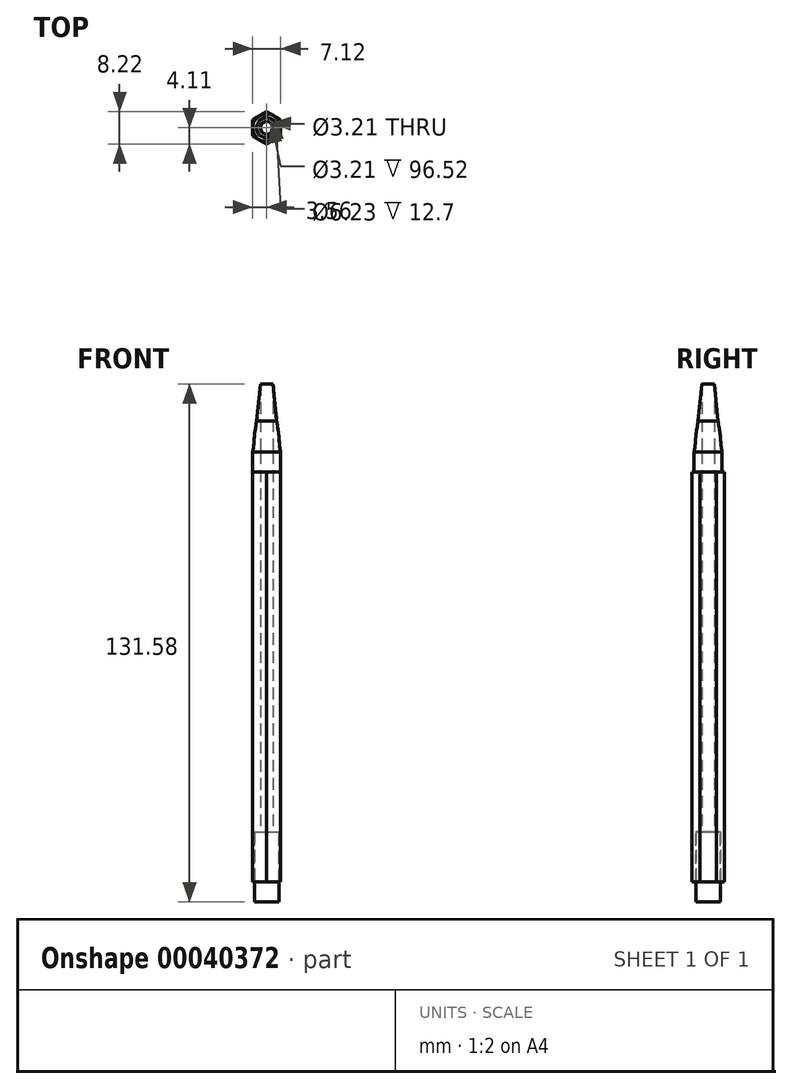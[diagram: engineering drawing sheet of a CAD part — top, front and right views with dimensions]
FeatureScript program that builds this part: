
annotation { "Feature Type Name" : "Feature", "Feature Type Description" : "" }
export const myFeature = defineFeature(function(context is Context, id is Id, definition is map)
    precondition{}
    {
        {
            var Q0;
            Q0=qCreatedBy(makeId("Top.planeOp"),FACE);
            var sketch = newSketch(context, id + "F0", { "sketchPlane" : qUnion([Q0])});
            skCircle(sketch, "E0.cCircle", {"center": v(0, 0) * mm, "radius": 3.56 * mm, "construction": true});
            skLineSegment(sketch, "E0.0", {"start": v(-3.56, 2.05) * mm, "end": v(0, 4.1) * mm});
            skLineSegment(sketch, "E0.1", {"start": v(0, 4.1) * mm, "end": v(3.55, 2.06) * mm});
            skLineSegment(sketch, "E0.2", {"start": v(3.55, 2.06) * mm, "end": v(3.56, -2.05) * mm});
            skLineSegment(sketch, "E0.3", {"start": v(3.56, -2.05) * mm, "end": v(0, -4.1) * mm});
            skLineSegment(sketch, "E0.4", {"start": v(0, -4.1) * mm, "end": v(-3.55, -2.06) * mm});
            skLineSegment(sketch, "E0.5", {"start": v(-3.55, -2.06) * mm, "end": v(-3.56, 2.05) * mm});
            skPoint(sketch, "E0.0.midPoint", {"position": v(-1.78, 3.08) * mm});
            skSolve(sketch);
        }
        {
            var Q0;
            Q0 = qSketchRegion(id + "F0", true);
            extrude(context, id + "F1", {"entities" : qUnion([Q0]), "depth" : 104.14 * mm});
        }
        {
            var Q0;
            Q0=makeQuery(id+"F1.opExtrude","CAP_FACE",FACE,{"disambiguationData":[OSD([sQuery(id+"F0.wireOp",EDGE,"E0.0"),sQuery(id+"F0.wireOp",EDGE,"E0.1"),sQuery(id+"F0.wireOp",EDGE,"E0.2"),sQuery(id+"F0.wireOp",EDGE,"E0.3"),sQuery(id+"F0.wireOp",EDGE,"E0.4"),sQuery(id+"F0.wireOp",EDGE,"E0.5")])],"isStart":false});
            var sketch = newSketch(context, id + "F2", { "sketchPlane" : qUnion([Q0])});
            skCircle(sketch, "E1", {"center": v(0, 0) * mm, "radius": 3.56 * mm});
            skSolve(sketch);
        }
        {
            var Q0;
            Q0 = qSketchRegion(id + "F2", true);
            extrude(context, id + "F3", {"entities" : qUnion([Q0]), "operationType" : NewBodyOperationType.ADD, "depth" : 5.08 * mm});
        }
        {
            var Q0;
            Q0=makeQuery(id+"F3.opExtrude","CAP_FACE",FACE,{"disambiguationData":[OSD([sQuery(id+"F2.wireOp",EDGE,"E1")])],"isStart":false});
            cPlane(context, id + "F4", {"entities" : qUnion([Q0]), "cplaneType" : CPlaneType.OFFSET, "offset" : 1.59 * mm, "width" : 152.4 * mm, "height" : 152.4 * mm});
        }
        {
            var Q0;
            Q0=qCreatedBy(id+"F4.planeOp",FACE);
            cPlane(context, id + "F5", {"entities" : qUnion([Q0]), "cplaneType" : CPlaneType.OFFSET, "offset" : 1.59 * mm, "width" : 152.4 * mm, "height" : 152.4 * mm});
        }
        {
            var Q0;
            Q0=qCreatedBy(id+"F5.planeOp",FACE);
            cPlane(context, id + "F6", {"entities" : qUnion([Q0]), "cplaneType" : CPlaneType.OFFSET, "offset" : 1.59 * mm, "width" : 152.4 * mm, "height" : 152.4 * mm});
        }
        {
            var Q0;
            Q0=qCreatedBy(id+"F6.planeOp",FACE);
            cPlane(context, id + "F7", {"entities" : qUnion([Q0]), "cplaneType" : CPlaneType.OFFSET, "offset" : 1.59 * mm, "width" : 152.4 * mm, "height" : 152.4 * mm});
        }
        {
            var Q0;
            Q0=qCreatedBy(id+"F7.planeOp",FACE);
            cPlane(context, id + "F8", {"entities" : qUnion([Q0]), "cplaneType" : CPlaneType.OFFSET, "offset" : 1.59 * mm, "width" : 152.4 * mm, "height" : 152.4 * mm});
        }
        {
            var Q0;
            Q0=qCreatedBy(id+"F8.planeOp",FACE);
            cPlane(context, id + "F9", {"entities" : qUnion([Q0]), "cplaneType" : CPlaneType.OFFSET, "offset" : 1.59 * mm, "width" : 152.4 * mm, "height" : 152.4 * mm});
        }
        {
            var Q0;
            Q0=qCreatedBy(id+"F9.planeOp",FACE);
            cPlane(context, id + "F10", {"entities" : qUnion([Q0]), "cplaneType" : CPlaneType.OFFSET, "offset" : 1.59 * mm, "width" : 152.4 * mm, "height" : 152.4 * mm});
        }
        {
            var Q0;
            Q0=qCreatedBy(id+"F10.planeOp",FACE);
            cPlane(context, id + "F11", {"entities" : qUnion([Q0]), "cplaneType" : CPlaneType.OFFSET, "offset" : 1.59 * mm, "width" : 152.4 * mm, "height" : 152.4 * mm});
        }
        {
            var Q0;
            Q0=qCreatedBy(id+"F11.planeOp",FACE);
            cPlane(context, id + "F12", {"entities" : qUnion([Q0]), "cplaneType" : CPlaneType.OFFSET, "offset" : 1.59 * mm, "width" : 152.4 * mm, "height" : 152.4 * mm});
        }
        {
            var Q0;
            Q0=qCreatedBy(id+"F12.planeOp",FACE);
            cPlane(context, id + "F13", {"entities" : qUnion([Q0]), "cplaneType" : CPlaneType.OFFSET, "offset" : 1.59 * mm, "width" : 152.4 * mm, "height" : 152.4 * mm});
        }
        {
            var Q0;
            Q0=qCreatedBy(id+"F13.planeOp",FACE);
            cPlane(context, id + "F14", {"entities" : qUnion([Q0]), "cplaneType" : CPlaneType.OFFSET, "offset" : 1.59 * mm, "width" : 152.4 * mm, "height" : 152.4 * mm});
        }
        {
            var Q0;
            Q0=qCreatedBy(id+"F14.planeOp",FACE);
            cPlane(context, id + "F15", {"entities" : qUnion([Q0]), "cplaneType" : CPlaneType.OFFSET, "offset" : 1.59 * mm, "width" : 152.4 * mm, "height" : 152.4 * mm});
        }
        {
            var Q0;
            Q0=qCreatedBy(id+"F15.planeOp",FACE);
            cPlane(context, id + "F16", {"entities" : qUnion([Q0]), "cplaneType" : CPlaneType.OFFSET, "offset" : 1.59 * mm, "width" : 152.4 * mm, "height" : 152.4 * mm});
        }
        {
            var Q0;
            Q0=qCreatedBy(id+"F16.planeOp",FACE);
            cPlane(context, id + "F17", {"entities" : qUnion([Q0]), "cplaneType" : CPlaneType.OFFSET, "offset" : 1.59 * mm, "width" : 152.4 * mm, "height" : 152.4 * mm});
        }
        {
            var Q0;
            Q0=qCreatedBy(id+"F17.planeOp",FACE);
            cPlane(context, id + "F18", {"entities" : qUnion([Q0]), "cplaneType" : CPlaneType.OFFSET, "offset" : 1.59 * mm, "width" : 152.4 * mm, "height" : 152.4 * mm});
        }
        {
            var Q0;
            Q0=qCreatedBy(id+"F18.planeOp",FACE);
            cPlane(context, id + "F19", {"entities" : qUnion([Q0]), "cplaneType" : CPlaneType.OFFSET, "offset" : 1.59 * mm, "width" : 152.4 * mm, "height" : 152.4 * mm});
        }
        {
            var Q0;
            Q0=qCreatedBy(id+"F4.planeOp",FACE);
            var sketch = newSketch(context, id + "F20", { "sketchPlane" : qUnion([Q0])});
            skCircle(sketch, "E2", {"center": v(0, 0) * mm, "radius": 3.3 * mm});
            skSolve(sketch);
        }
        {
            var Q0;
            Q0=qCreatedBy(id+"F5.planeOp",FACE);
            var sketch = newSketch(context, id + "F21", { "sketchPlane" : qUnion([Q0])});
            skCircle(sketch, "E3", {"center": v(0, 0) * mm, "radius": 3.18 * mm});
            skSolve(sketch);
        }
        {
            var Q0;
            Q0=qCreatedBy(id+"F6.planeOp",FACE);
            var sketch = newSketch(context, id + "F22", { "sketchPlane" : qUnion([Q0])});
            skCircle(sketch, "E4", {"center": v(0, 0) * mm, "radius": 3.05 * mm});
            skSolve(sketch);
        }
        {
            var Q0;
            Q0=qCreatedBy(id+"F6.planeOp",FACE);
            var sketch = newSketch(context, id + "F23", { "sketchPlane" : qUnion([Q0])});
            skCircle(sketch, "E5", {"center": v(0, 0) * mm, "radius": 2.92 * mm});
            skSolve(sketch);
        }
        {
            var Q0;
            Q0=qCreatedBy(id+"F7.planeOp",FACE);
            var sketch = newSketch(context, id + "F24", { "sketchPlane" : qUnion([Q0])});
            skCircle(sketch, "E6", {"center": v(0, 0) * mm, "radius": 2.8 * mm});
            skSolve(sketch);
        }
        {
            var Q0;
            Q0=qCreatedBy(id+"F8.planeOp",FACE);
            var sketch = newSketch(context, id + "F25", { "sketchPlane" : qUnion([Q0])});
            skCircle(sketch, "E7", {"center": v(0, 0) * mm, "radius": 2.54 * mm});
            skSolve(sketch);
        }
        {
            var Q0;
            Q0=makeQuery(id+"F3.opExtrude","CAP_FACE",FACE,{"disambiguationData":[OSD([sQuery(id+"F2.wireOp",EDGE,"E1")])],"isStart":false});
            var Q1;
            Q1=makeQuery(id+"F20.imprint","IMPRINT",FACE,{"disambiguationData":[TD([[makeQuery(id+"F20.imprint","IMPRINT",EDGE,{"derivedFrom":sQuery(id+"F20.wireOp",EDGE,"E2")}),1.0]])]});
            var Q2;
            Q2=makeQuery(id+"F21.imprint","IMPRINT",FACE,{"disambiguationData":[TD([[makeQuery(id+"F21.imprint","IMPRINT",EDGE,{"derivedFrom":sQuery(id+"F21.wireOp",EDGE,"E3")}),1.0]])]});
            var Q3;
            Q3=makeQuery(id+"F22.imprint","IMPRINT",FACE,{"disambiguationData":[TD([[makeQuery(id+"F22.imprint","IMPRINT",EDGE,{"derivedFrom":sQuery(id+"F22.wireOp",EDGE,"E4")}),1.0]])]});
            var Q4;
            Q4=makeQuery(id+"F24.imprint","IMPRINT",FACE,{"disambiguationData":[TD([[makeQuery(id+"F24.imprint","IMPRINT",EDGE,{"derivedFrom":sQuery(id+"F24.wireOp",EDGE,"E6")}),1.0]])]});
            var Q5;
            Q5=makeQuery(id+"F25.imprint","IMPRINT",FACE,{"disambiguationData":[TD([[makeQuery(id+"F25.imprint","IMPRINT",EDGE,{"derivedFrom":sQuery(id+"F25.wireOp",EDGE,"E7")}),1.0]])]});
            loft(context, id + "F26", {"sheetProfilesArray" : [{ "sheetProfileEntities" : qUnion([Q0]) }, { "sheetProfileEntities" : qUnion([Q1]) }, { "sheetProfileEntities" : qUnion([Q2]) }, { "sheetProfileEntities" : qUnion([Q3]) }, { "sheetProfileEntities" : qUnion([Q4]) }, { "sheetProfileEntities" : qUnion([Q5]) }]});
        }
        {
            var Q0;
            Q0=qCreatedBy(id+"F19.planeOp",FACE);
            var sketch = newSketch(context, id + "F27", { "sketchPlane" : qUnion([Q0])});
            skCircle(sketch, "E8", {"center": v(0, 0) * mm, "radius": 0.8 * mm});
            skSolve(sketch);
        }
        {
            var Q1;
            Q1=makeQuery(id+"F26.opLoft","CAP_FACE",FACE,{"disambiguationData":[OSD([makeQuery(id+"F25.imprint","IMPRINT",FACE,{"disambiguationData":[TD([[makeQuery(id+"F25.imprint","IMPRINT",EDGE,{"derivedFrom":sQuery(id+"F25.wireOp",EDGE,"E7")}),1.0]])]})])],"isStart":true});
            var Q2;
            Q2=makeQuery(id+"F27.imprint","IMPRINT",FACE,{"disambiguationData":[TD([[makeQuery(id+"F27.imprint","IMPRINT",EDGE,{"derivedFrom":sQuery(id+"F27.wireOp",EDGE,"E8")}),1.0]])]});
            loft(context, id + "F28", {"operationType" : NewBodyOperationType.ADD, "sheetProfilesArray" : [{ "sheetProfileEntities" : qUnion([Q1]) }, { "sheetProfileEntities" : qUnion([Q2]) }]});
        }
        {
            var Q0;
            Q0=makeQuery(id+"F28.opLoft","CAP_FACE",FACE,{"disambiguationData":[OSD([makeQuery(id+"F27.imprint","IMPRINT",FACE,{"disambiguationData":[TD([[makeQuery(id+"F27.imprint","IMPRINT",EDGE,{"derivedFrom":sQuery(id+"F27.wireOp",EDGE,"E8")}),1.0]])]})])],"isStart":true});
            var sketch = newSketch(context, id + "F29", { "sketchPlane" : qUnion([Q0])});
            skCircle(sketch, "E9", {"center": v(0, 0) * mm, "radius": 0.47 * mm});
            skSolve(sketch);
        }
        {
            var Q0;
            Q0 = qSketchRegion(id + "F29", true);
            extrude(context, id + "F30", {"entities" : qUnion([Q0]), "operationType" : NewBodyOperationType.REMOVE, "endBound" : BoundingType.THROUGH_ALL, "oppositeDirection" : true, "depth" : 25.4 * mm});
        }
        {
            var Q0;
            Q0=makeQuery(id+"F23.imprint","IMPRINT",FACE,{"disambiguationData":[TD([[makeQuery(id+"F23.imprint","IMPRINT",EDGE,{"derivedFrom":sQuery(id+"F23.wireOp",EDGE,"E5")}),1.0]])]});
            var sketch = newSketch(context, id + "F31", { "sketchPlane" : qUnion([Q0])});
            skCircle(sketch, "E10", {"center": v(0, 0) * mm, "radius": 0.46 * mm});
            skSolve(sketch);
        }
        {
            var Q0;
            Q0 = qSketchRegion(id + "F31", true);
            extrude(context, id + "F32", {"entities" : qUnion([Q0]), "operationType" : NewBodyOperationType.REMOVE, "endBound" : BoundingType.THROUGH_ALL, "oppositeDirection" : true, "depth" : 25.4 * mm});
        }
        {
            var Q0;
            Q0=makeQuery(id+"F1.opExtrude","CAP_FACE",FACE,{"disambiguationData":[OSD([sQuery(id+"F0.wireOp",EDGE,"E0.0"),sQuery(id+"F0.wireOp",EDGE,"E0.1"),sQuery(id+"F0.wireOp",EDGE,"E0.2"),sQuery(id+"F0.wireOp",EDGE,"E0.3"),sQuery(id+"F0.wireOp",EDGE,"E0.4"),sQuery(id+"F0.wireOp",EDGE,"E0.5")])],"isStart":true});
            var sketch = newSketch(context, id + "F33", { "sketchPlane" : qUnion([Q0])});
            skCircle(sketch, "E11", {"center": v(0, 0) * mm, "radius": 1.6 * mm});
            skSolve(sketch);
        }
        {
            var Q0;
            Q0 = qSketchRegion(id + "F33", true);
            extrude(context, id + "F34", {"entities" : qUnion([Q0]), "operationType" : NewBodyOperationType.REMOVE, "endBound" : BoundingType.THROUGH_ALL, "oppositeDirection" : true, "depth" : 25.4 * mm});
        }
        {
            var Q0;
            Q0=makeQuery(id+"F1.opExtrude","CAP_FACE",FACE,{"disambiguationData":[OSD([sQuery(id+"F0.wireOp",EDGE,"E0.0"),sQuery(id+"F0.wireOp",EDGE,"E0.1"),sQuery(id+"F0.wireOp",EDGE,"E0.2"),sQuery(id+"F0.wireOp",EDGE,"E0.3"),sQuery(id+"F0.wireOp",EDGE,"E0.4"),sQuery(id+"F0.wireOp",EDGE,"E0.5")])],"isStart":true});
            var sketch = newSketch(context, id + "F35", { "sketchPlane" : qUnion([Q0])});
            skCircle(sketch, "E12", {"center": v(0, 0) * mm, "radius": 3.12 * mm});
            skSolve(sketch);
        }
        {
            var Q0;
            Q0 = qSketchRegion(id + "F35", true);
            extrude(context, id + "F36", {"entities" : qUnion([Q0]), "operationType" : NewBodyOperationType.REMOVE, "oppositeDirection" : true, "depth" : 12.7 * mm});
        }
        {
            var Q0;
            Q0=makeQuery(id+"F36.boolean.opBoolean","COPY",FACE,{"derivedFrom":makeQuery(id+"F36.opExtrude","CAP_FACE",FACE,{"disambiguationData":[OSD([sQuery(id+"F35.wireOp",EDGE,"E12")])],"isStart":false})});
            var sketch = newSketch(context, id + "F37", { "sketchPlane" : qUnion([Q0])});
            skSolve(sketch);
        }
        {
            var Q0;
            {var subQ0=sQuery(id+"F35.wireOp",EDGE,"E12");Q0=makeQuery(id+"F37.imprint","IMPRINT",FACE,{"disambiguationData":[TD([[makeQuery(id+"F37.imprint","IMPRINT",EDGE,{"derivedFrom":makeQuery(id+"F36.boolean.opBoolean","COPY",EDGE,{"derivedFrom":makeQuery(id+"F36.opExtrude","CAP_EDGE",EDGE,{"disambiguationData":[OSD([subQ0])],"isStart":false})})}),1.0]])]});}
            var sketch = newSketch(context, id + "F38", { "sketchPlane" : qUnion([Q0])});
            skCircle(sketch, "E13", {"center": v(0, 0) * mm, "radius": 3.1 * mm});
            skSolve(sketch);
        }
        {
            var Q0;
            Q0 = qSketchRegion(id + "F38", true);
            extrude(context, id + "F39", {"entities" : qUnion([Q0]), "operationType" : NewBodyOperationType.ADD, "depth" : 17.78 * mm});
        }
    });
